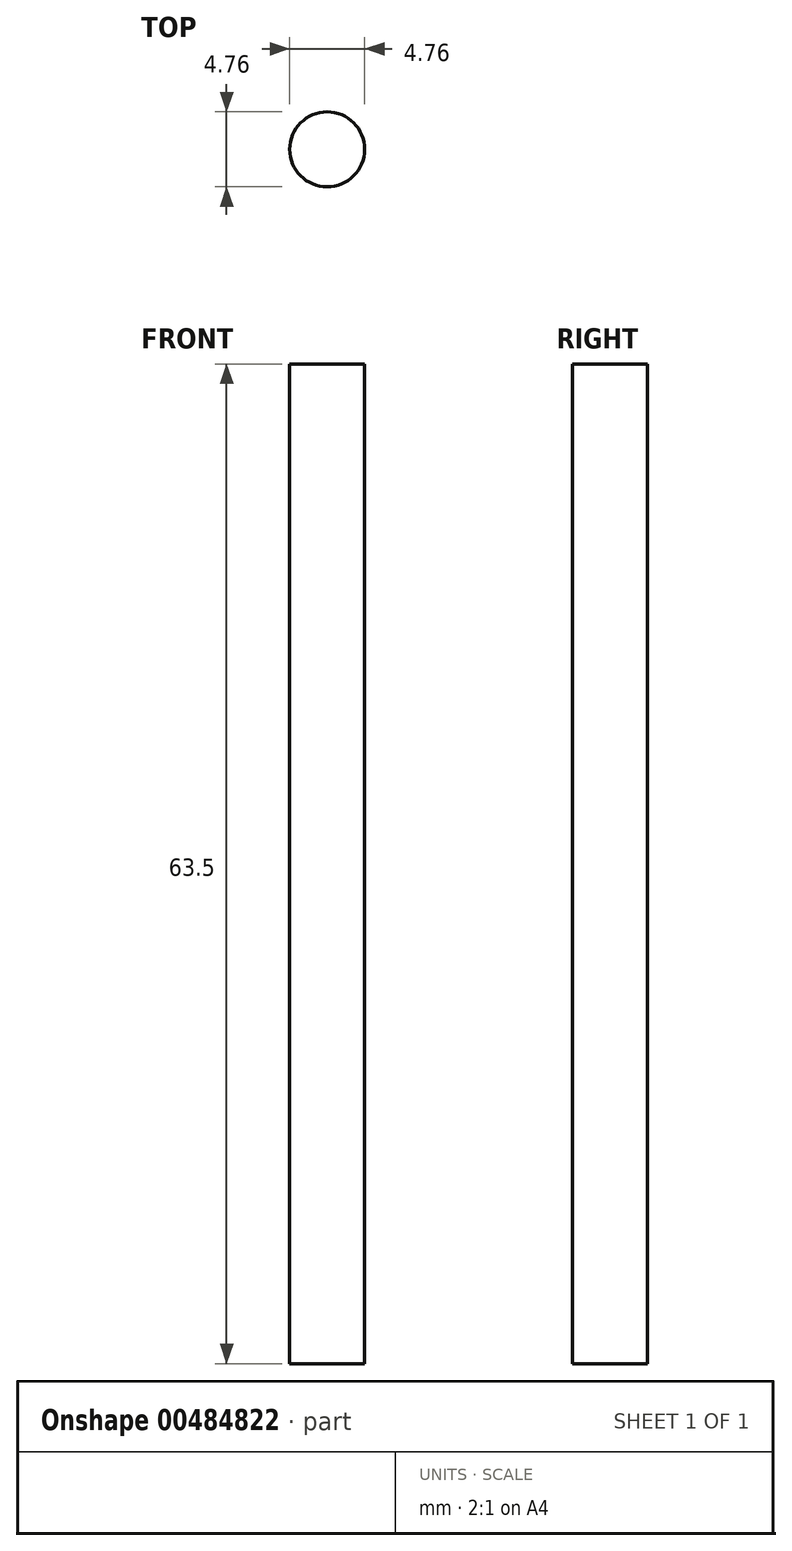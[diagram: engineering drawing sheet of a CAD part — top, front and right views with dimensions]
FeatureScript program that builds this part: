
annotation { "Feature Type Name" : "Feature", "Feature Type Description" : "" }
export const myFeature = defineFeature(function(context is Context, id is Id, definition is map)
    precondition{}
    {
        {
            var Q0;
            Q0=qCreatedBy(makeId("Top.planeOp"),FACE);
            var sketch = newSketch(context, id + "F0", { "sketchPlane" : qUnion([Q0])});
            skCircle(sketch, "E0", {"center": v(0, 0) * mm, "radius": 2.38 * mm});
            skSolve(sketch);
        }
        {
            var Q0;
            Q0 = qSketchRegion(id + "F0", true);
            extrude(context, id + "F1", {"entities" : qUnion([Q0]), "depth" : 63.5 * mm, "symmetric" : true});
        }
    });
